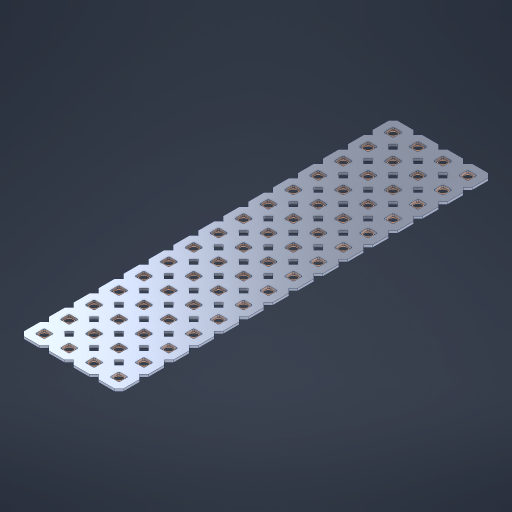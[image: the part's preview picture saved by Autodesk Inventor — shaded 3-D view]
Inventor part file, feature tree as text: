
AUTODESK INVENTOR PART (.ipt)
format: ipt  version: 2023 (Build 270158000, 158)  size: 956,928 bytes
history: native  units: in
note: dims shown in document units (in); Inventor stores cm internally (conversion verified against a paired STEP export)
features: other x61, extrude x59, sketch x2, pattern_linear x1
ambient origin geometry x8: Origin, YZ Plane, XZ Plane, XY Plane, X Axis, Y Axis, Z Axis, Center Point
bodies: Solid1 (feature_tree), Body (feature_tree)
feature tree (123):
  pattern_linear  "Rectangular Pattern1"  Spacing1=0.09in  [1 undecoded]
  sketch  "Sketch1"  dims[d1=0.5in]
  sketch  "Sketch2"  dims[d2=0.182in d3=0.09in d4=0.09in d5=0.09in d6=0.09in d7=0.09in d8=0.09in d9=0.09in d10=0.09in d11=0.02in d13=0.0in d14=0.172in d15=0.0625in d16=0.0in d19=0.5in d22=0.5in]
  other  "Srf1"
  other  "Srf126"
  other  "Srf127"
  other  "Srf128"
  other  "Srf129"
  other  "Srf130"
  other  "Srf131"
  other  "Srf250"
  other  "Srf251"
  other  "Srf252"
  other  "Srf253"
  other  "Srf254"
  other  "Srf255"
  other  "Srf256"
  other  "Srf257"
  other  "Srf268"
  other  "Srf269"
  other  "Srf270"
  other  "Srf271"
  other  "Srf272"
  other  "Srf273"
  other  "Srf274"
  other  "Srf275"
  other  "Srf276"
  other  "Srf277"
  other  "Srf278"
  other  "Srf279"
  other  "Srf280"
  other  "Srf281"
  other  "Srf282"
  other  "Srf293"
  other  "Srf294"
  other  "Srf295"
  other  "Srf296"
  other  "Srf297"
  other  "Srf298"
  other  "Srf299"
  other  "Srf300"
  other  "Srf301"
  other  "Srf302"
  other  "Srf303"
  other  "Srf304"
  other  "Srf305"
  other  "Srf306"
  other  "Srf307"
  other  "Srf318"
  other  "Srf319"
  other  "Srf320"
  other  "Srf321"
  other  "Srf322"
  other  "Srf323"
  other  "Srf324"
  other  "Srf325"
  other  "Srf326"
  other  "Srf327"
  other  "Srf328"
  other  "Srf329"
  other  "Srf330"
  other  "Srf331"
  other  "Srf332"
  other  "Circle"
  extrude  "ExtrusionSrf126"  Depth=0.09in
  extrude  "ExtrusionSrf127"  Depth=0.09in
  extrude  "ExtrusionSrf128"  Depth=0.09in
  extrude  "ExtrusionSrf129"  Depth=0.09in
  extrude  "ExtrusionSrf130"  Depth=0.09in
  extrude  "ExtrusionSrf131"  Depth=0.09in
  extrude  "ExtrusionSrf250"  Depth=0.09in
  extrude  "ExtrusionSrf251"  Depth=0.02in
  extrude  "ExtrusionSrf252"  TaperAngle=0.0deg  [1 undecoded]
  extrude  "ExtrusionSrf253"  Depth=0.5in
  extrude  "ExtrusionSrf254"  Depth=0.5in TaperAngle=0.0deg
  extrude  "ExtrusionSrf255"  Depth=0.5in
  extrude  "ExtrusionSrf256"  Depth=0.5in
  extrude  "ExtrusionSrf257"  [1 undecoded]
  extrude  "ExtrusionSrf268"  [1 undecoded]
  extrude  "ExtrusionSrf269"  [1 undecoded]
  extrude  "ExtrusionSrf270"  [1 undecoded]
  extrude  "ExtrusionSrf271"  [1 undecoded]
  extrude  "ExtrusionSrf272"  [1 undecoded]
  extrude  "ExtrusionSrf273"  [1 undecoded]
  extrude  "ExtrusionSrf274"  [1 undecoded]
  extrude  "ExtrusionSrf275"  [1 undecoded]
  extrude  "ExtrusionSrf276"  [1 undecoded]
  extrude  "ExtrusionSrf277"  [1 undecoded]
  extrude  "ExtrusionSrf278"  [1 undecoded]
  extrude  "ExtrusionSrf279"  [1 undecoded]
  extrude  "ExtrusionSrf280"  [1 undecoded]
  extrude  "ExtrusionSrf281"  [1 undecoded]
  extrude  "ExtrusionSrf282"  [1 undecoded]
  extrude  "ExtrusionSrf293"  [1 undecoded]
  extrude  "ExtrusionSrf294"  [1 undecoded]
  extrude  "ExtrusionSrf295"  [1 undecoded]
  extrude  "ExtrusionSrf296"  [1 undecoded]
  extrude  "ExtrusionSrf297"  [1 undecoded]
  extrude  "ExtrusionSrf298"  [1 undecoded]
  extrude  "ExtrusionSrf299"  [1 undecoded]
  extrude  "ExtrusionSrf300"  [1 undecoded]
  extrude  "ExtrusionSrf301"  [1 undecoded]
  extrude  "ExtrusionSrf302"  [1 undecoded]
  extrude  "ExtrusionSrf303"  [1 undecoded]
  extrude  "ExtrusionSrf304"  [1 undecoded]
  extrude  "ExtrusionSrf305"  [1 undecoded]
  extrude  "ExtrusionSrf306"  [1 undecoded]
  extrude  "ExtrusionSrf307"  [1 undecoded]
  extrude  "ExtrusionSrf318"  [1 undecoded]
  extrude  "ExtrusionSrf319"  [1 undecoded]
  extrude  "ExtrusionSrf320"  [1 undecoded]
  extrude  "ExtrusionSrf321"  [1 undecoded]
  extrude  "ExtrusionSrf322"  [1 undecoded]
  extrude  "ExtrusionSrf323"  [1 undecoded]
  extrude  "ExtrusionSrf324"  [1 undecoded]
  extrude  "ExtrusionSrf325"  [1 undecoded]
  extrude  "ExtrusionSrf326"  [1 undecoded]
  extrude  "ExtrusionSrf327"  [1 undecoded]
  extrude  "ExtrusionSrf328"  [1 undecoded]
  extrude  "ExtrusionSrf329"  [1 undecoded]
  extrude  "ExtrusionSrf330"  [1 undecoded]
  extrude  "ExtrusionSrf331"  [1 undecoded]
  extrude  "ExtrusionSrf332"  [1 undecoded]
note: 48 required parameter values undecoded (feature->parameter linkage not recoverable at this tier; creation-order binding heuristic only, values carry confidence <= 0.55)
